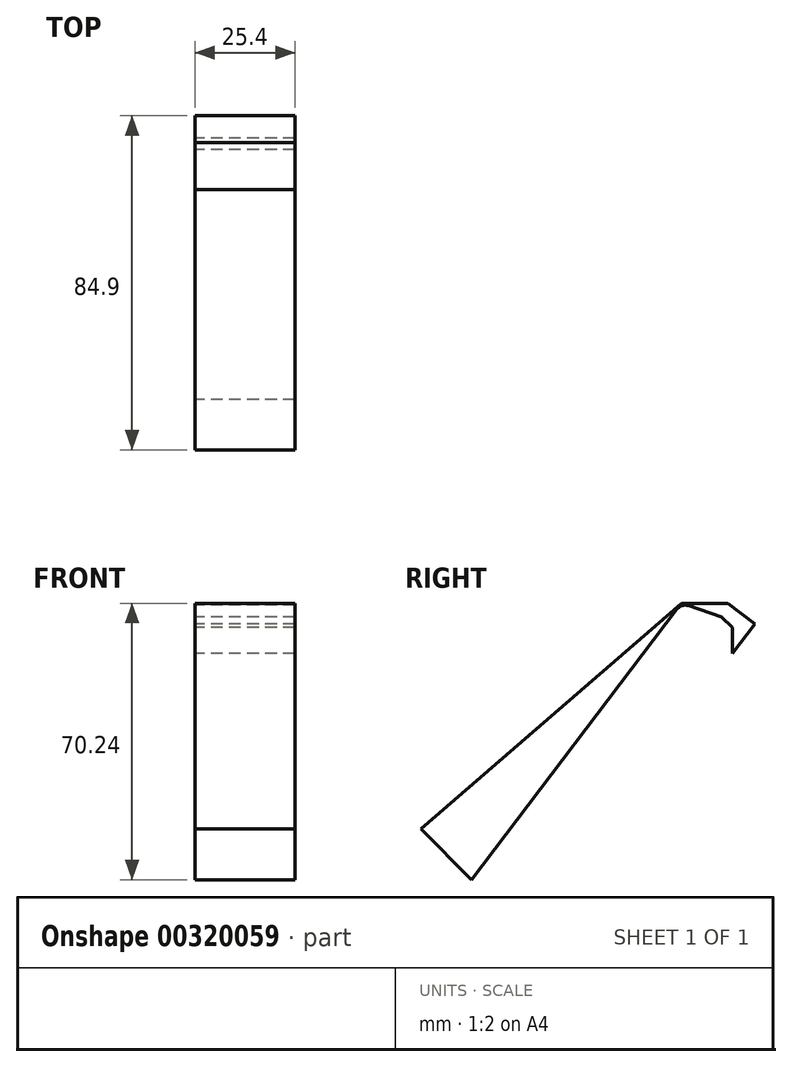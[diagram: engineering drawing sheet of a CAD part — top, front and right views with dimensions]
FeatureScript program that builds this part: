
annotation { "Feature Type Name" : "Feature", "Feature Type Description" : "" }
export const myFeature = defineFeature(function(context is Context, id is Id, definition is map)
    precondition{}
    {
        {
            var Q0;
            Q0=qCreatedBy(makeId("Right.planeOp"),FACE);
            var sketch = newSketch(context, id + "F0", { "sketchPlane" : qUnion([Q0])});
            skLineSegment(sketch, "E0", {"start": v(-66.17, -26.48) * mm, "end": v(0, 30.77) * mm});
            skLineSegment(sketch, "E1", {"start": v(-53.35, -39.47) * mm, "end": v(-1.1, 29.31) * mm});
            skLineSegment(sketch, "E2", {"start": v(-53.35, -39.47) * mm, "end": v(-66.17, -26.48) * mm});
            skLineSegment(sketch, "E3", {"start": v(0, 30.77) * mm, "end": v(11.85, 30.77) * mm});
            skLineSegment(sketch, "E4", {"start": v(11.85, 30.77) * mm, "end": v(18.73, 25.55) * mm});
            skLineSegment(sketch, "E5", {"start": v(18.73, 25.55) * mm, "end": v(13.01, 18.02) * mm});
            skLineSegment(sketch, "E6", {"start": v(13.01, 18.02) * mm, "end": v(13.01, 24.62) * mm});
            skLineSegment(sketch, "E7", {"start": v(13.01, 24.62) * mm, "end": v(10.11, 27.35) * mm});
            skLineSegment(sketch, "E8", {"start": v(10.11, 27.35) * mm, "end": v(1.73, 30.18) * mm});
            skPoint(sketch, "E9.visualSharp", {"position": v(0, 30.77) * mm});
            skArc(sketch, "E9.filletArc", {"start": v(1.73, 30.18) * mm, "mid": v(0.17, 30.2) * mm, "end": v(-1.1, 29.31) * mm});
            skSolve(sketch);
        }
        {
            var Q0;
            Q0=makeQuery(id+"F0.imprint","IMPRINT",FACE,{"disambiguationData":[TD([[makeQuery(id+"F0.imprint","IMPRINT",EDGE,{"derivedFrom":sQuery(id+"F0.wireOp",EDGE,"E0")}),-1.0]])]});
            extrude(context, id + "F1", {"entities" : qUnion([Q0]), "depth" : 25.4 * mm});
        }
        {
            var Q0;
            Q0=makeQuery(id+"F0.imprint","IMPRINT",FACE,{"disambiguationData":[TD([[makeQuery(id+"F0.imprint","IMPRINT",EDGE,{"derivedFrom":sQuery(id+"F0.wireOp",EDGE,"E3")}),-1.0]])]});
            extrude(context, id + "F2", {"entities" : qUnion([Q0]), "depth" : 25.4 * mm});
        }
    });
